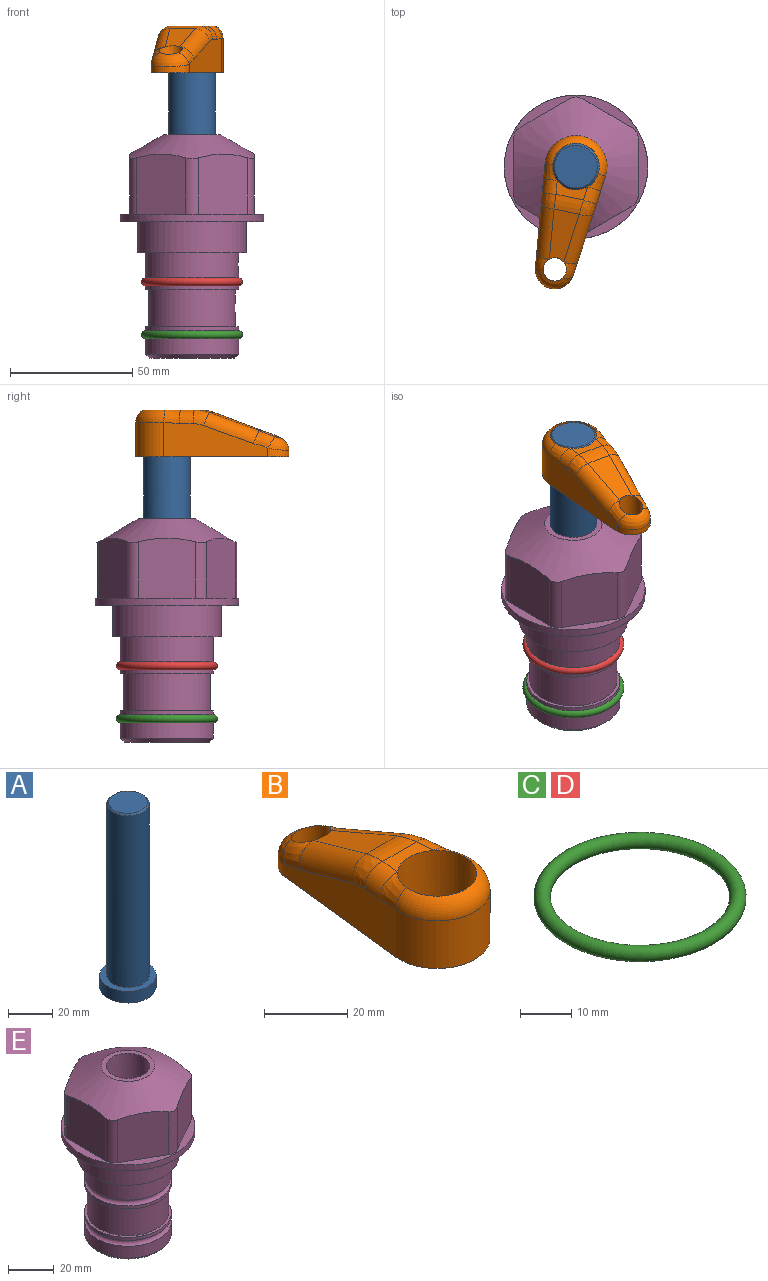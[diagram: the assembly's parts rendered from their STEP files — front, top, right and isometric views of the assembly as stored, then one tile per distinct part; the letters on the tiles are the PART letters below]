
ASSEMBLY  parts=5 mates=3
PART A: 6 faces, bbox 25.4x25.4x101.6 mm
  f0: plane 17.46x17.46mm, normal (0,0,1), area 239.5mm2, adj f5
  f1: plane 25.4x25.4mm, normal (0,0,-1), area 506.7mm2, adj f2
  f2: cylinder r=12.7mm len=25.4mm, axis (0,0,1), area 506.7mm2, adj f1,f3
  f3: plane 25.4x25.4mm, normal (0,0,1), area 221.7mm2, adj f2,f4
  f4: cylinder r=9.53mm len=94.46mm, axis (0,0,1), area 5653mm2, adj f3,f5
  f5: cone r=8.73mm half-angle=45deg, axis (0,0,-1), area 64.4mm2, adj f0,f4
PART B: 22 faces, bbox 28.3x65.3x20.4 mm
  f0: cylinder r=12.7mm len=25.4mm, axis (0,0,-1), area 598.6mm2, adj f1,f3,f7,f10
  f1: plane 42.34x14.01mm, normal (0.99,0.11,0), area 430.7mm2, adj f0,f2,f7,f11,f13,f15,f17,f19
  f2: cylinder r=7.94mm len=15.78mm, axis (0,0,-1), area 64.7mm2, adj f1,f3,f7,f21
  f3: plane 42.34x14.01mm, normal (-0.99,0.11,0), area 430.7mm2, adj f0,f2,f7,f12,f14,f16,f18,f20
  f4: cylinder r=9.53mm len=19.05mm, axis (0,0,-1), area 1140.1mm2, adj f6,f7,f10,f11,f12
  f5: cylinder r=4.76mm len=10.58mm, axis (0,0,-1), area 274mm2, adj f7,f8,f19,f20,f21
  f6: plane 12.73x5.65mm, normal (0,0,1), area 47.1mm2, adj f4,f9,f13,f14
  f7: plane 63.5x25.4mm, normal (0,0,-1), area 886.1mm2, adj f0,f1,f2,f3,f4,f5
  f8: plane 21.11x11.3mm, normal (0,0.34,0.94), area 174.1mm2, adj f5,f9,f17,f18
  f9: cylinder r=17.78mm len=11.46mm, axis (-1,0,0), area 68.3mm2, adj f6,f8,f15,f16
  f10: torus R=7.11mm, axis (0,0,1), area 245.1mm2, adj f0,f4,f11,f12
  f11: bspline ~8.68x6.87mm, area 45.1mm2, adj f1,f4,f10,f13
  f12: bspline ~8.68x6.87mm, area 45.1mm2, adj f3,f4,f10,f14
  f13: cylinder r=5.59mm len=6.27mm, axis (0.11,-0.99,0), area 49.9mm2, adj f1,f6,f11,f15
  f14: cylinder r=5.59mm len=6.27mm, axis (0.11,0.99,0), area 49.9mm2, adj f3,f6,f12,f16
  f15: bspline ~6.32x6.16mm, area 47.8mm2, adj f1,f9,f13,f17
  f16: bspline ~11.1x6.74mm, area 47.8mm2, adj f3,f9,f14,f18
  f17: cylinder r=5.59mm len=21.7mm, axis (0.1,-0.93,0.34), area 186.4mm2, adj f1,f8,f15,f19
  f18: cylinder r=5.59mm len=21.7mm, axis (0.1,0.93,-0.34), area 186.4mm2, adj f3,f8,f16,f20
  f19: bspline ~8.9x7.42mm, area 45.9mm2, adj f1,f5,f17,f21
  f20: bspline ~8.9x7.42mm, area 45.9mm2, adj f3,f5,f18,f21
  f21: bspline ~15.87x7.94mm, area 108mm2, adj f2,f5,f19,f20
PART C: 1 faces, bbox 44.7x44.7x3.2 mm
  f0: torus R=19.05mm, axis (0,0,1), area 1193.9mm2
PART D: same geometry as C
PART E: 36 faces, bbox 58.7x58.7x91.2 mm
  f0: cylinder r=17.78mm len=35.56mm, axis (0,0,1), area 1670.8mm2, adj f23,f24,f31
  f1: cylinder r=19.05mm len=38.1mm, axis (0,0,1), area 1191.9mm2, adj f26,f27,f30
  f2: plane 58.66x58.66mm, normal (0,0,-1), area 1150.6mm2, adj f3,f28
  f3: cylinder r=29.33mm len=58.66mm, axis (0,0,-1), area 585.1mm2, adj f2,f4
  f4: plane 58.66x58.66mm, normal (0,0,1), area 475.9mm2, adj f3,f5,f6,f7,f8,f9,f10,f11
  f5: plane 24.5x20.32mm, normal (-0.5,0.87,0), area 562.8mm2, adj f4,f15,f16,f17
  f6: plane 24.5x20.32mm, normal (0.5,0.87,0), area 562.8mm2, adj f4,f14,f15,f17
  f7: plane 24.5x23.48mm, normal (1,0,0), area 562.8mm2, adj f4,f13,f14,f17
  f8: plane 24.5x20.32mm, normal (0.5,-0.87,0), area 562.8mm2, adj f4,f12,f13,f17
  f9: plane 24.5x20.32mm, normal (-0.5,-0.87,0), area 562.8mm2, adj f4,f11,f12,f17
  f10: plane 24.5x23.48mm, normal (-1,0,0), area 562.8mm2, adj f4,f11,f16,f17
  f11: cylinder r=5.08mm len=23.01mm, axis (0,0,-1), area 121.2mm2, adj f4,f9,f10,f17
  f12: cylinder r=5.08mm len=23.01mm, axis (0,0,-1), area 121.2mm2, adj f4,f8,f9,f17
  f13: cylinder r=5.08mm len=23.01mm, axis (0,0,-1), area 121.2mm2, adj f4,f7,f8,f17
  f14: cylinder r=5.08mm len=23.01mm, axis (0,0,-1), area 121.2mm2, adj f4,f6,f7,f17
  f15: cylinder r=5.08mm len=23.01mm, axis (0,0,-1), area 121.2mm2, adj f4,f5,f6,f17
  f16: cylinder r=5.08mm len=23.01mm, axis (0,0,-1), area 121.2mm2, adj f4,f5,f10,f17
  f17: cone r=11.73mm half-angle=60deg, axis (0,0,-1), area 2071.8mm2, adj f5,f6,f7,f8,f9,f10,f11,f12
  f18: plane 23.46x23.46mm, normal (0,0,1), area 147.4mm2, adj f17,f35
  f19: plane 34.93x34.93mm, normal (0,0,-1), area 958mm2, adj f29
  f20: cylinder r=19.05mm len=38.1mm, axis (0,0,1), area 760.1mm2, adj f21,f29
  f21: torus R=19.05mm, axis (0,0,1), area 565.3mm2, adj f20,f22
  f22: cylinder r=19.05mm len=38.1mm, axis (0,0,1), area 190mm2, adj f21,f23
  f23: plane 38.1x38.1mm, normal (0,0,1), area 146.9mm2, adj f0,f22
  f24: plane 38.1x38.1mm, normal (0,0,-1), area 146.9mm2, adj f0,f25
  f25: cylinder r=19.05mm len=38.1mm, axis (0,0,1), area 190mm2, adj f24,f26
  f26: torus R=19.05mm, axis (0,0,1), area 565.3mm2, adj f1,f25
  f27: plane 44.45x44.45mm, normal (0,0,-1), area 411.7mm2, adj f1,f28
  f28: cylinder r=22.23mm len=44.45mm, axis (0,0,1), area 1773.5mm2, adj f2,f27
  f29: cone r=19.05mm half-angle=45deg, axis (0,0,1), area 257.5mm2, adj f19,f20
  f30: cylinder r=3.17mm len=6.75mm, axis (-1,0,0), area 128mm2, adj f1,f33
  f31: cylinder r=3.17mm len=6.35mm, axis (-1,0,0), area 102.5mm2, adj f0,f33
  f32: plane 25.4x25.4mm, normal (0,0,1), area 506.7mm2, adj f33
  f33: cylinder r=12.7mm len=66.42mm, axis (0,0,-1), area 5236.2mm2, adj f30,f31,f32,f34
  f34: cone r=9.53mm half-angle=30deg, axis (0,0,-1), area 443.4mm2, adj f33,f35
  f35: cylinder r=9.53mm len=19.05mm, axis (0,0,-1), area 849mm2, adj f18,f34
PLACE A rot(axis=(0,0,-1),101.7deg) t=(0,0,6.38)mm
PLACE B rot(axis=(0,0,1),168.3deg) t=(0,0,60.99)mm
PLACE C t=(0,0,-21.59)mm
PLACE D at identity
PLACE E at identity fixed
MATE fastened C.f0 <-> E.f0  axis (0,0,1) through (0,0,-46.1)mm
MATE cylindrical A.f2 <-> E.f0  axis (0,0,1) through (0,0,32.01)mm
MATE fastened B.f0 <-> A.f2  axis (0,0,1) through (0,0,80.04)mm
